# Revit family: 304_Cim787(OT)-_
name_source: partatom
category: Pipe Accessories
revit_build: Autodesk Revit 2017 (Build: 20160225_1515(x64)
units: mm (PartAtom-declared; Revit-internal decimal feet)

## family parameters
Always vertical = Yes
Cut with Voids When Loaded = No
Part Type = Valve - Breaks Into
Round Connector Dimension = Use Diameter
Shared = No
Work Plane-Based = No

## types (6) — shared parameters
CAT0 = Yes
DD3 = 32 mm
DD4 = 25 mm  [stored 0.082021 ft]
Description = BALANCING VALVE - VARIABLE ORIFICE - PN 25
F = 50 mm
HH3 = 3 mm  [stored 0.00984252 ft]
HH6 = 17 mm  [stored 0.0557743 ft]
HH7 = 19 mm  [stored 0.062336 ft]
L2D_Min = 3048 mm
Manufacturer = Cimberio
QmdConnectorList = 301;D;302;D
URL = www.cimberio.it
magiPartTypeId = 304
magiProductFamilyId = Cim787(OT)-*
zero-valued in all types: MC_Default_elevation

## per-type parameters (varying)
| type | CenSd_R1_6 | D | DD1 | DD2 | DL | DL__ve | HH1 | HH2 | HH4 | HH5 | L2D | LL1 | LL2 | LL2__ve | LL3 | LL3__ve | LL4 | R | R1 | W2D | WW1 |
| Cim787(OT)-15 | 8 mm  [stored 0.0262467 ft] | 15 mm | 17 mm  [stored 0.0557743 ft] | 24 mm  [stored 0.0787402 ft] | 16 mm  [stored 0.0524934 ft] | -16 mm  [stored -0.0524934 ft] | 7 mm  [stored 0.0229659 ft] | 12 mm  [stored 0.0393701 ft] | 28 mm | 16 mm  [stored 0.0524934 ft] | 75 mm | 38 mm | 12 mm  [stored 0.0393701 ft] | -12 mm  [stored -0.0393701 ft] | 2 mm  [stored 0.00656168 ft] | -2 mm  [stored -0.00656168 ft] | 12 mm  [stored 0.0393701 ft] | 8 mm  [stored 0.0262467 ft] | 9 mm  [stored 0.0295276 ft] | 15 mm  [stored 0.0492126 ft] | 9 mm  [stored 0.0295276 ft] |
| Cim787(OT)-50 | 26 mm | 50 mm | 29 mm | 40 mm | 26 mm | -26 mm  [stored -0.0853018 ft] | 22 mm  [stored 0.0721785 ft] | 41 mm | 24 mm  [stored 0.0787402 ft] | 18 mm  [stored 0.0590551 ft] | 124 mm | 62 mm | 20 mm  [stored 0.0656168 ft] | -20 mm | 3 mm  [stored 0.00984252 ft] | -3 mm | 20 mm  [stored 0.0656168 ft] | 25 mm  [stored 0.082021 ft] | 30 mm | 50 mm | 16 mm  [stored 0.0524934 ft] |
| Cim787(OT)-40 | 21 mm  [stored 0.0688976 ft] | 40 mm | 26 mm | 37 mm | 23 mm  [stored 0.0754593 ft] | -23 mm  [stored -0.0754593 ft] | 18 mm  [stored 0.0590551 ft] | 33 mm | 27 mm | 18 mm  [stored 0.0590551 ft] | 115 mm | 58 mm | 18 mm  [stored 0.0590551 ft] | -18 mm | 4 mm | -4 mm | 18 mm  [stored 0.0590551 ft] | 20 mm  [stored 0.0656168 ft] | 24 mm  [stored 0.0787402 ft] | 40 mm | 14 mm  [stored 0.0459318 ft] |
| Cim787(OT)-32 | 17 mm  [stored 0.0557743 ft] | 32 mm | 25 mm  [stored 0.082021 ft] | 35 mm | 22 mm  [stored 0.0721785 ft] | -22 mm  [stored -0.0721785 ft] | 14 mm  [stored 0.0459318 ft] | 26 mm | 30 mm | 18 mm  [stored 0.0590551 ft] | 108 mm | 54 mm | 17 mm  [stored 0.0557743 ft] | -17 mm | 3 mm  [stored 0.00984252 ft] | -3 mm | 17 mm  [stored 0.0557743 ft] | 16 mm  [stored 0.0524934 ft] | 19 mm  [stored 0.062336 ft] | 32 mm | 14 mm  [stored 0.0459318 ft] |
| Cim787(OT)-25 | 13 mm | 25 mm | 20 mm  [stored 0.0656168 ft] | 28 mm | 21 mm  [stored 0.0688976 ft] | -21 mm  [stored -0.0688976 ft] | 11 mm  [stored 0.0360892 ft] | 21 mm  [stored 0.0688976 ft] | 27 mm | 17 mm  [stored 0.0557743 ft] | 87 mm | 44 mm | 14 mm  [stored 0.0459318 ft] | -14 mm | 1 mm  [stored 0.00328084 ft] | -1 mm  [stored -0.00328084 ft] | 14 mm  [stored 0.0459318 ft] | 13 mm | 15 mm  [stored 0.0492126 ft] | 25 mm  [stored 0.082021 ft] | 11 mm  [stored 0.0360892 ft] |
| Cim787(OT)-20 | 10 mm  [stored 0.0328084 ft] | 20 mm | 18 mm  [stored 0.0590551 ft] | 26 mm | 19 mm  [stored 0.062336 ft] | -19 mm  [stored -0.062336 ft] | 9 mm  [stored 0.0295276 ft] | 16 mm  [stored 0.0524934 ft] | 28 mm | 16 mm  [stored 0.0524934 ft] | 80 mm | 40 mm | 13 mm | -13 mm | 0 mm  [stored 0 ft] | 0 mm  [stored 0 ft] | 13 mm | 10 mm  [stored 0.0328084 ft] | 12 mm  [stored 0.0393701 ft] | 20 mm  [stored 0.0656168 ft] | 10 mm  [stored 0.0328084 ft] |

note: column(s) folded — value = type name in every type: magiProductCode, magiProductId

note: [stored X ft] marks values corroborated as IEEE doubles in the binary element streams (Revit-internal decimal feet)

## geometry (parser evidence)
native form markers: Sweep x2
no freeform markers — native parametric forms only
